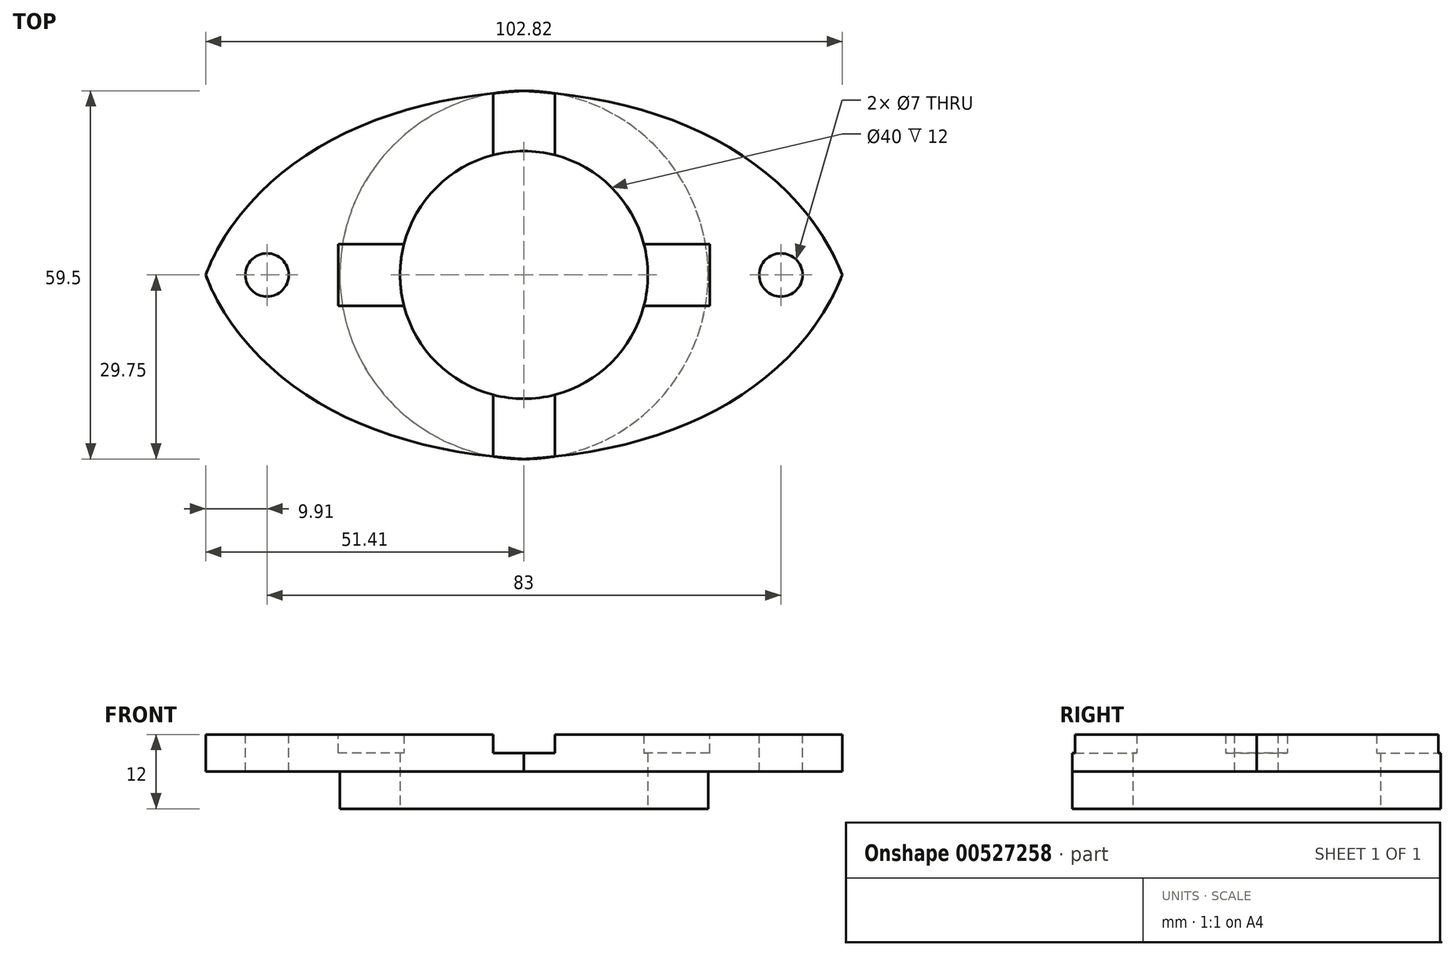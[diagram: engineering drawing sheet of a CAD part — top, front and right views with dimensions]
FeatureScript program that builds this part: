
annotation { "Feature Type Name" : "Feature", "Feature Type Description" : "" }
export const myFeature = defineFeature(function(context is Context, id is Id, definition is map)
    precondition{}
    {
        {
            var Q0;
            Q0=qCreatedBy(makeId("Top.planeOp"),FACE);
            var sketch = newSketch(context, id + "F0", { "sketchPlane" : qUnion([Q0])});
            skCircle(sketch, "E0", {"center": v(0, 0) * mm, "radius": 29.75 * mm});
            skSolve(sketch);
        }
        {
            var Q0;
            Q0=makeQuery(id+"F0.imprint","IMPRINT",FACE,{"disambiguationData":[TD([[makeQuery(id+"F0.imprint","IMPRINT",EDGE,{"derivedFrom":sQuery(id+"F0.wireOp",EDGE,"E0")}),1.0]])]});
            extrude(context, id + "F1", {"entities" : qUnion([Q0]), "depth" : 6 * mm, "offsetDistance" : 25 * mm});
        }
        {
            var Q0;
            Q0=qCreatedBy(makeId("Top.planeOp"),FACE);
            var sketch = newSketch(context, id + "F2", { "sketchPlane" : qUnion([Q0])});
            skCircle(sketch, "E1", {"center": v(0, 0) * mm, "radius": 18.95 * mm});
            skSolve(sketch);
        }
        {
            var Q0;
            Q0=sQuery(id+"F2.wireOp",VERTEX,"E1.center");
            var Q1;
            Q1=makeQuery(id+"F1.opExtrude","SWEPT_BODY",BODY,{"disambiguationData":[OSD([sQuery(id+"F0.wireOp",EDGE,"E0")])]});
            hole(context, id + "F3", {"style" : HoleStyle.SIMPLE, "endStyle" : HoleEndStyle.THROUGH, "oppositeDirection" : true, "holeDiameter" : 40 * mm, "isTappedThrough" : true, "tappedDepth" : 12 * mm, "tapClearance" : 3, "locations" : qUnion([Q0]), "scope" : qUnion([Q1])});
        }
        {
            var Q0;
            Q0=makeQuery(id+"F1.opExtrude","CAP_FACE",FACE,{"disambiguationData":[OSD([sQuery(id+"F0.wireOp",EDGE,"E0")])],"isStart":false});
            var sketch = newSketch(context, id + "F4", { "sketchPlane" : qUnion([Q0])});
            skFitSpline(sketch, "E2", {"points": [v(-51.4, 0) * mm, v(-34.52, 19.78) * mm, v(0, 29.75) * mm], "startDerivative": vector(19.74, 51.8) * mm, "endDerivative": vector(76.26, 4.4) * mm});
            skFitSpline(sketch, "E3.MirrorCS", {"points": [v(51.4, 0) * mm, v(34.52, 19.78) * mm, v(0, 29.75) * mm], "startDerivative": vector(-19.74, 51.8) * mm, "endDerivative": vector(-76.26, 4.4) * mm});
            skFitSpline(sketch, "E4.MirrorCS", {"points": [v(51.4, 0) * mm, v(34.52, -19.78) * mm, v(0, -29.75) * mm], "startDerivative": vector(-19.74, -51.8) * mm, "endDerivative": vector(-76.26, -4.4) * mm});
            skFitSpline(sketch, "E5.MirrorCS", {"points": [v(-51.4, 0) * mm, v(-34.52, -19.78) * mm, v(0, -29.75) * mm], "startDerivative": vector(19.74, -51.8) * mm, "endDerivative": vector(76.26, -4.4) * mm});
            skSolve(sketch);
        }
        {
            var Q0;
            Q0 = qSketchRegion(id + "F4", true);
            extrude(context, id + "F5", {"entities" : qUnion([Q0]), "operationType" : NewBodyOperationType.ADD, "depth" : 6 * mm, "offsetDistance" : 25 * mm});
        }
        {
            var Q0;
            Q0=makeQuery(id+"F5.opExtrude","CAP_FACE",FACE,{"disambiguationData":[OSD([sQuery(id+"F4.wireOp",EDGE,"E2"),sQuery(id+"F4.wireOp",EDGE,"E3.MirrorCS"),sQuery(id+"F4.wireOp",EDGE,"E4.MirrorCS"),sQuery(id+"F4.wireOp",EDGE,"E5.MirrorCS")])],"isStart":false});
            var sketch = newSketch(context, id + "F6", { "sketchPlane" : qUnion([Q0])});
            skCircle(sketch, "E6", {"center": v(0, 0) * mm, "radius": 20 * mm});
            skSolve(sketch);
        }
        {
            var Q0;
            Q0=sQuery(id+"F6.wireOp",VERTEX,"E6.center");
            var Q1;
            Q1=makeQuery(id+"F1.opExtrude","SWEPT_BODY",BODY,{"disambiguationData":[OSD([sQuery(id+"F0.wireOp",EDGE,"E0")])]});
            hole(context, id + "F7", {"style" : HoleStyle.SIMPLE, "endStyle" : HoleEndStyle.THROUGH, "holeDiameter" : 40 * mm, "isTappedThrough" : true, "tappedDepth" : 12 * mm, "tapClearance" : 3, "locations" : qUnion([Q0]), "scope" : qUnion([Q1])});
        }
        {
            var Q0;
            Q0=makeQuery(id+"F5.opExtrude","CAP_FACE",FACE,{"disambiguationData":[OSD([sQuery(id+"F4.wireOp",EDGE,"E2"),sQuery(id+"F4.wireOp",EDGE,"E3.MirrorCS"),sQuery(id+"F4.wireOp",EDGE,"E4.MirrorCS"),sQuery(id+"F4.wireOp",EDGE,"E5.MirrorCS")])],"isStart":false});
            var sketch = newSketch(context, id + "F8", { "sketchPlane" : qUnion([Q0])});
            skCircle(sketch, "E7", {"center": v(41.5, 0) * mm, "radius": 3.53 * mm});
            skCircle(sketch, "E8.MirrorC", {"center": v(-41.5, 0) * mm, "radius": 3.53 * mm});
            skSolve(sketch);
        }
        {
            var Q0;
            Q0=sQuery(id+"F8.wireOp",VERTEX,"E8.MirrorC.center");
            var Q1;
            Q1=sQuery(id+"F8.wireOp",VERTEX,"E7.center");
            var Q2;
            Q2=makeQuery(id+"F1.opExtrude","SWEPT_BODY",BODY,{"disambiguationData":[OSD([sQuery(id+"F0.wireOp",EDGE,"E0")])]});
            hole(context, id + "F9", {"style" : HoleStyle.SIMPLE, "endStyle" : HoleEndStyle.THROUGH, "holeDiameter" : 7 * mm, "isTappedThrough" : true, "tappedDepth" : 12 * mm, "tapClearance" : 3, "locations" : qUnion([Q0, Q1]), "scope" : qUnion([Q2])});
        }
        {
            var Q0;
            Q0=makeQuery(id+"F5.opExtrude","CAP_FACE",FACE,{"disambiguationData":[OSD([sQuery(id+"F4.wireOp",EDGE,"E2"),sQuery(id+"F4.wireOp",EDGE,"E3.MirrorCS"),sQuery(id+"F4.wireOp",EDGE,"E4.MirrorCS"),sQuery(id+"F4.wireOp",EDGE,"E5.MirrorCS")])],"isStart":false});
            var sketch = newSketch(context, id + "F10", { "sketchPlane" : qUnion([Q0])});
            skLineSegment(sketch, "E9.bottom", {"start": v(5, -32.59) * mm, "end": v(-5, -32.59) * mm});
            skLineSegment(sketch, "E9.top", {"start": v(5, 32.59) * mm, "end": v(-5, 32.59) * mm});
            skLineSegment(sketch, "E9.left", {"start": v(5, -32.59) * mm, "end": v(5, 32.59) * mm});
            skLineSegment(sketch, "E9.right", {"start": v(-5, -32.59) * mm, "end": v(-5, 32.59) * mm});
            skPoint(sketch, "E9.middle", {"position": v(0, 0) * mm});
            skSolve(sketch);
        }
        {
            var Q0;
            Q0 = qSketchRegion(id + "F10", true);
            extrude(context, id + "F11", {"entities" : qUnion([Q0]), "operationType" : NewBodyOperationType.REMOVE, "oppositeDirection" : true, "depth" : 3 * mm, "offsetDistance" : 25 * mm});
        }
        {
            var Q0;
            {var subQ0=sQuery(id+"F4.wireOp",EDGE,"E3.MirrorCS");var subQ1=sQuery(id+"F4.wireOp",EDGE,"E4.MirrorCS");Q0=makeQuery(id+"F11.boolean.opBoolean","SPLIT",FACE,{"disambiguationData":[TD([makeQuery(id+"F5.opExtrude","SWEPT_FACE",FACE,{"disambiguationData":[OSD([subQ0])]})])],"derivedFrom":makeQuery(id+"F5.opExtrude","CAP_FACE",FACE,{"disambiguationData":[OSD([sQuery(id+"F4.wireOp",EDGE,"E2"),subQ0,subQ1,sQuery(id+"F4.wireOp",EDGE,"E5.MirrorCS")])],"isStart":false})});}
            var sketch = newSketch(context, id + "F12", { "sketchPlane" : qUnion([Q0])});
            skLineSegment(sketch, "E10.bottom", {"start": v(30, -5) * mm, "end": v(-30, -5) * mm});
            skLineSegment(sketch, "E10.top", {"start": v(30, 5) * mm, "end": v(-30, 5) * mm});
            skLineSegment(sketch, "E10.left", {"start": v(30, -5) * mm, "end": v(30, 5) * mm});
            skLineSegment(sketch, "E10.right", {"start": v(-30, -5) * mm, "end": v(-30, 5) * mm});
            skPoint(sketch, "E10.middle", {"position": v(0, 0) * mm});
            skSolve(sketch);
        }
        {
            var Q0;
            Q0 = qSketchRegion(id + "F12", true);
            extrude(context, id + "F13", {"entities" : qUnion([Q0]), "operationType" : NewBodyOperationType.REMOVE, "oppositeDirection" : true, "depth" : 3 * mm, "offsetDistance" : 25 * mm});
        }
    });
